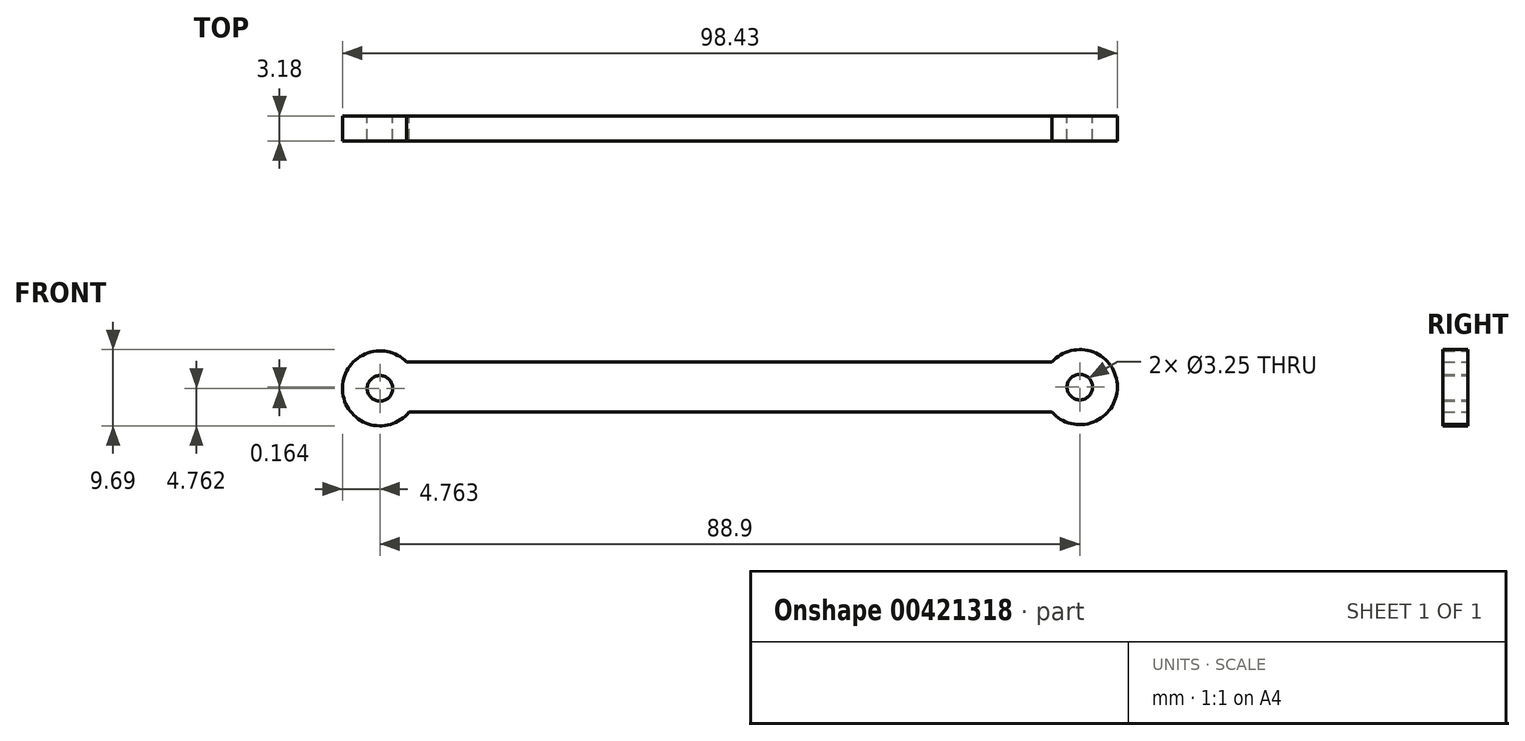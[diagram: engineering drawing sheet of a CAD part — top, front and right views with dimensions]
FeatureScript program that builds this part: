
annotation { "Feature Type Name" : "Feature", "Feature Type Description" : "" }
export const myFeature = defineFeature(function(context is Context, id is Id, definition is map)
    precondition{}
    {
        {
            var Q0;
            Q0=qCreatedBy(makeId("Front.planeOp"),FACE);
            var sketch = newSketch(context, id + "F0", { "sketchPlane" : qUnion([Q0])});
            skCircle(sketch, "E0", {"center": v(-102.53, 26.4) * mm, "radius": 1.63 * mm});
            skArc(sketch, "E1", {"start": v(-99.13, 29.73) * mm, "mid": v(-107.28, 26.17) * mm, "end": v(-98.84, 23.38) * mm});
            skCircle(sketch, "E2", {"center": v(-13.63, 26.56) * mm, "radius": 1.63 * mm});
            skArc(sketch, "E3", {"start": v(-17.18, 23.38) * mm, "mid": v(-8.86, 26.56) * mm, "end": v(-17.18, 29.73) * mm});
            skLineSegment(sketch, "E4", {"start": v(-99.13, 29.73) * mm, "end": v(-17.18, 29.73) * mm});
            skLineSegment(sketch, "E5", {"start": v(-17.18, 23.38) * mm, "end": v(-98.84, 23.38) * mm});
            skSolve(sketch);
        }
        {
            var Q0;
            Q0=makeQuery(id+"F0.imprint","IMPRINT",FACE,{"disambiguationData":[TD([[makeQuery(id+"F0.imprint","IMPRINT",EDGE,{"derivedFrom":sQuery(id+"F0.wireOp",EDGE,"E0")}),-1.0]])]});
            extrude(context, id + "F1", {"entities" : qUnion([Q0]), "depth" : 3.17 * mm});
        }
    });
